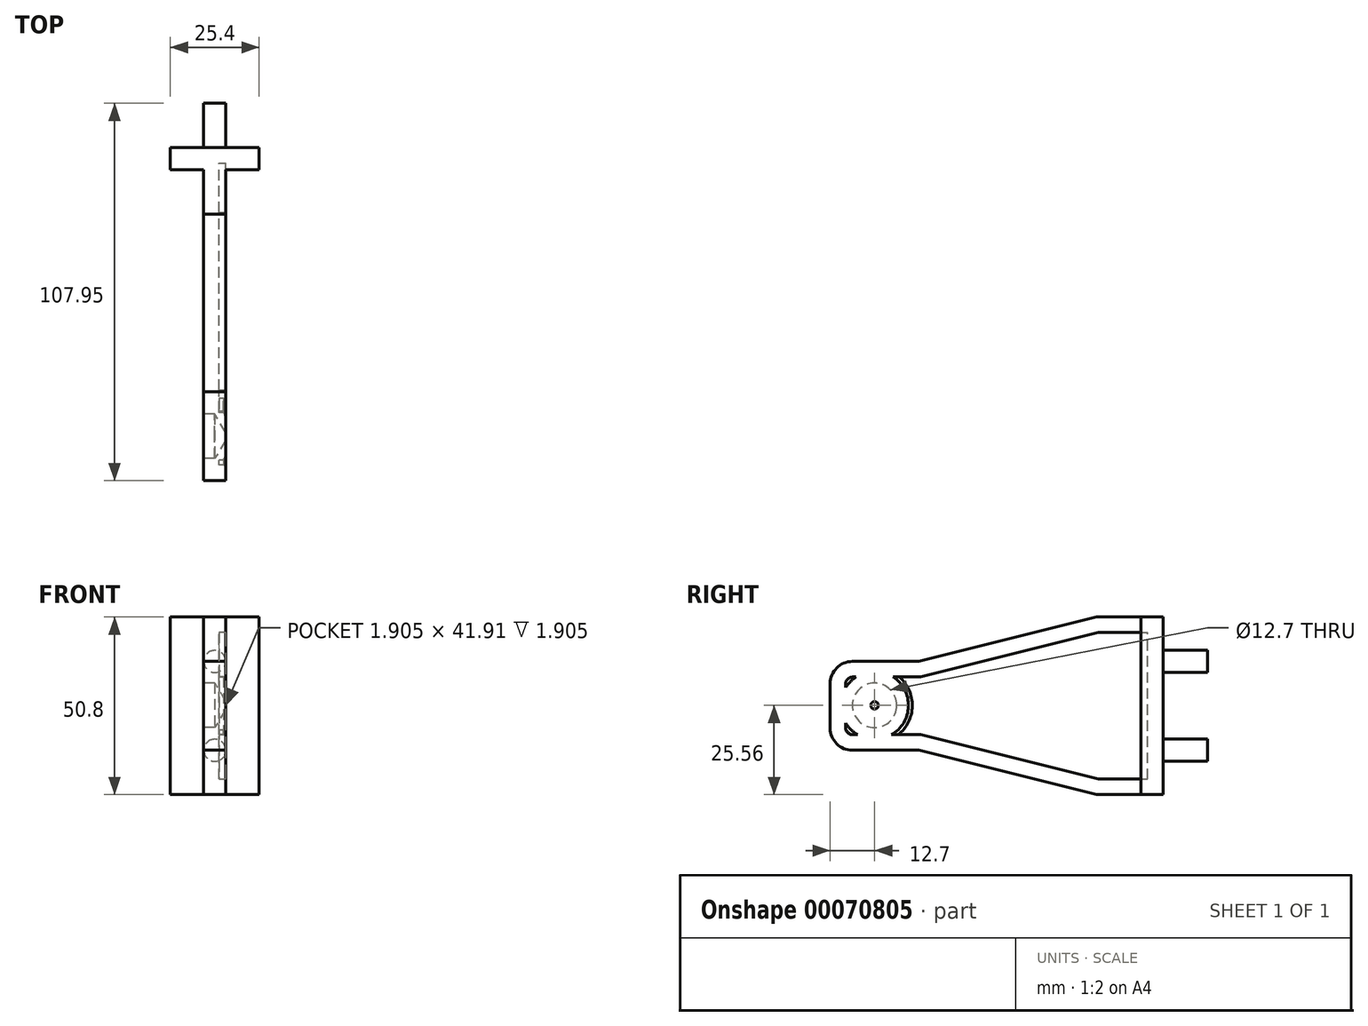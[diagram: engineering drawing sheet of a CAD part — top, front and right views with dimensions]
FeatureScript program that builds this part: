
annotation { "Feature Type Name" : "Feature", "Feature Type Description" : "" }
export const myFeature = defineFeature(function(context is Context, id is Id, definition is map)
    precondition{}
    {
        {
            var Q0;
            Q0=qCreatedBy(makeId("Front.planeOp"),FACE);
            var sketch = newSketch(context, id + "F0", { "sketchPlane" : qUnion([Q0])});
            skLineSegment(sketch, "E0.bottom", {"start": v(0, 0) * mm, "end": v(25.4, 0) * mm});
            skLineSegment(sketch, "E0.top", {"start": v(0, 50.8) * mm, "end": v(25.4, 50.8) * mm});
            skLineSegment(sketch, "E0.left", {"start": v(0, 0) * mm, "end": v(0, 50.8) * mm});
            skLineSegment(sketch, "E0.right", {"start": v(25.4, 0) * mm, "end": v(25.4, 50.8) * mm});
            skSolve(sketch);
        }
        {
            var Q0;
            Q0=makeQuery(id+"F0.imprint","IMPRINT",FACE,{"disambiguationData":[TD([[makeQuery(id+"F0.imprint","IMPRINT",EDGE,{"derivedFrom":sQuery(id+"F0.wireOp",EDGE,"E0.bottom")}),1.0]])]});
            extrude(context, id + "F1", {"entities" : qUnion([Q0]), "depth" : 6.35 * mm});
        }
        {
            var Q0;
            Q0=makeQuery(id+"F1.opExtrude","CAP_FACE",FACE,{"disambiguationData":[OSD([sQuery(id+"F0.wireOp",EDGE,"E0.bottom"),sQuery(id+"F0.wireOp",EDGE,"E0.top"),sQuery(id+"F0.wireOp",EDGE,"E0.left"),sQuery(id+"F0.wireOp",EDGE,"E0.right")])],"isStart":false});
            var sketch = newSketch(context, id + "F2", { "sketchPlane" : qUnion([Q0])});
            skLineSegment(sketch, "E1.bottom", {"start": v(9.53, 50.8) * mm, "end": v(15.88, 50.8) * mm});
            skLineSegment(sketch, "E1.top", {"start": v(9.53, 0) * mm, "end": v(15.88, 0) * mm});
            skLineSegment(sketch, "E1.left", {"start": v(9.53, 50.8) * mm, "end": v(9.53, 0) * mm});
            skLineSegment(sketch, "E1.right", {"start": v(15.88, 50.8) * mm, "end": v(15.88, 0) * mm});
            skSolve(sketch);
        }
        {
            var Q0;
            Q0=makeQuery(id+"F2.imprint","IMPRINT",FACE,{"disambiguationData":[TD([[makeQuery(id+"F2.imprint","IMPRINT",EDGE,{"derivedFrom":sQuery(id+"F2.wireOp",EDGE,"E1.bottom")}),-1.0]])]});
            extrude(context, id + "F3", {"entities" : qUnion([Q0]), "operationType" : NewBodyOperationType.ADD, "depth" : 12.7 * mm});
        }
        {
            var Q0;
            Q0=makeQuery(id+"F3.opExtrude","CAP_FACE",FACE,{"disambiguationData":[OSD([sQuery(id+"F2.wireOp",EDGE,"E1.bottom"),sQuery(id+"F2.wireOp",EDGE,"E1.top"),sQuery(id+"F2.wireOp",EDGE,"E1.left"),sQuery(id+"F2.wireOp",EDGE,"E1.right")])],"isStart":false});
            cPlane(context, id + "F4", {"entities" : qUnion([Q0]), "cplaneType" : CPlaneType.OFFSET, "offset" : 50.8 * mm, "width" : 152.4 * mm, "height" : 152.4 * mm});
        }
        {
            var Q0;
            Q0=qCreatedBy(id+"F4.planeOp",FACE);
            var sketch = newSketch(context, id + "F5", { "sketchPlane" : qUnion([Q0])});
            skLineSegment(sketch, "E2.0", {"start": v(9.53, 38.1) * mm, "end": v(9.53, 12.7) * mm});
            skLineSegment(sketch, "E3.0", {"start": v(15.88, 38.1) * mm, "end": v(15.88, 12.7) * mm});
            skLineSegment(sketch, "E4", {"start": v(9.53, 38.1) * mm, "end": v(15.88, 38.1) * mm});
            skLineSegment(sketch, "E5", {"start": v(9.53, 12.7) * mm, "end": v(15.88, 12.7) * mm});
            skSolve(sketch);
        }
        {
            var Q0;
            Q0=makeQuery(id+"F3.opExtrude","CAP_FACE",FACE,{"disambiguationData":[OSD([sQuery(id+"F2.wireOp",EDGE,"E1.bottom"),sQuery(id+"F2.wireOp",EDGE,"E1.top"),sQuery(id+"F2.wireOp",EDGE,"E1.left"),sQuery(id+"F2.wireOp",EDGE,"E1.right")])],"isStart":false});
            var Q1;
            Q1=makeQuery(id+"F5.imprint","IMPRINT",FACE,{"disambiguationData":[TD([[makeQuery(id+"F5.imprint","IMPRINT",EDGE,{"derivedFrom":sQuery(id+"F5.wireOp",EDGE,"E2.0")}),1.0]])]});
            loft(context, id + "F6", {"operationType" : NewBodyOperationType.ADD, "sheetProfilesArray" : [{ "sheetProfileEntities" : qUnion([Q0]) }, { "sheetProfileEntities" : qUnion([Q1]) }]});
        }
        {
            var Q0;
            Q0=makeQuery(id+"F6.opLoft","CAP_FACE",FACE,{"disambiguationData":[OSD([makeQuery(id+"F5.imprint","IMPRINT",FACE,{"disambiguationData":[TD([[makeQuery(id+"F5.imprint","IMPRINT",EDGE,{"derivedFrom":sQuery(id+"F5.wireOp",EDGE,"E2.0")}),1.0]])]})])],"isStart":true});
            extrude(context, id + "F7", {"entities" : qUnion([Q0]), "operationType" : NewBodyOperationType.ADD, "depth" : 25.4 * mm});
        }
        {
            var Q0;
            Q0=makeQuery(id+"F7.opExtrude","CAP_EDGE",EDGE,{"disambiguationData":[OSD([sQuery(id+"F5.wireOp",EDGE,"E2.0"),sQuery(id+"F5.wireOp",EDGE,"E3.0"),sQuery(id+"F5.wireOp",EDGE,"E4")])],"isStart":false});
            var Q1;
            Q1=makeQuery(id+"F7.opExtrude","CAP_EDGE",EDGE,{"disambiguationData":[OSD([sQuery(id+"F5.wireOp",EDGE,"E2.0"),sQuery(id+"F5.wireOp",EDGE,"E3.0"),sQuery(id+"F5.wireOp",EDGE,"E5")])],"isStart":false});
            fillet(context, id + "F8", {"entities" : qUnion([Q0, Q1]), "radius" : 6.35 * mm, "tangentPropagation" : true, "allowEdgeOverflow" : false});
        }
        {
            var Q0;
            {var subQ0=sQuery(id+"F5.wireOp",EDGE,"E5");var subQ1=sQuery(id+"F5.wireOp",EDGE,"E4");var subQ2=sQuery(id+"F5.wireOp",EDGE,"E2.0");var subQ3=sQuery(id+"F2.wireOp",EDGE,"E1.left");Q0=makeQuery(id+"F7.boolean.opBoolean","MERGE",FACE,{"derivedFrom":[makeQuery(id+"F6.boolean.opBoolean","MERGE",FACE,{"derivedFrom":[makeQuery(id+"F3.opExtrude","SWEPT_FACE",FACE,{"disambiguationData":[OSD([subQ3])]}),makeQuery(id+"F6.opLoft","SWEPT_FACE",FACE,{"disambiguationData":[OSD([sQuery(id+"F0.wireOp",EDGE,"E0.bottom"),sQuery(id+"F0.wireOp",EDGE,"E0.top"),sQuery(id+"F2.wireOp",EDGE,"E1.bottom"),sQuery(id+"F2.wireOp",EDGE,"E1.top"),subQ3,subQ2,subQ1,subQ0])]})]}),makeQuery(id+"F7.opExtrude","SWEPT_FACE",FACE,{"disambiguationData":[OSD([subQ2,subQ1,subQ0])]})]});}
            var sketch = newSketch(context, id + "F9", { "sketchPlane" : qUnion([Q0])});
            skPoint(sketch, "E6", {"position": v(95.25, 25.4) * mm});
            skPoint(sketch, "E7", {"position": v(82.55, 25.56) * mm});
            skSolve(sketch);
        }
        {
            var Q0;
            Q0=sQuery(id+"F9.wireOp",VERTEX,"E7");
            var Q1;
            Q1=makeQuery(id+"F1.opExtrude","SWEPT_BODY",BODY,{"disambiguationData":[OSD([sQuery(id+"F0.wireOp",EDGE,"E0.bottom"),sQuery(id+"F0.wireOp",EDGE,"E0.top"),sQuery(id+"F0.wireOp",EDGE,"E0.left"),sQuery(id+"F0.wireOp",EDGE,"E0.right")])]});
            hole(context, id + "F10", {"style" : HoleStyle.SIMPLE, "holeDiameter" : 12.7 * mm, "endStyle" : HoleEndStyle.BLIND, "holeDepth" : 3.17 * mm, "locations" : qUnion([Q0]), "scope" : qUnion([Q1])});
        }
        {
            var Q0;
            Q0=makeQuery(id+"F1.opExtrude","CAP_FACE",FACE,{"disambiguationData":[OSD([sQuery(id+"F0.wireOp",EDGE,"E0.bottom"),sQuery(id+"F0.wireOp",EDGE,"E0.top"),sQuery(id+"F0.wireOp",EDGE,"E0.left"),sQuery(id+"F0.wireOp",EDGE,"E0.right")])],"isStart":true});
            var sketch = newSketch(context, id + "F11", { "sketchPlane" : qUnion([Q0])});
            skCircle(sketch, "E8", {"center": v(-12.7, 38.1) * mm, "radius": 3.18 * mm});
            skPoint(sketch, "E8.centerSnap0", {"position": v(-12.7, 50.8) * mm});
            skCircle(sketch, "E9", {"center": v(-12.7, 12.7) * mm, "radius": 3.18 * mm});
            skPoint(sketch, "E9.centerSnap0", {"position": v(-12.7, 0) * mm});
            skSolve(sketch);
        }
        {
            var Q0;
            Q0=makeQuery(id+"F11.imprint","IMPRINT",FACE,{"disambiguationData":[TD([[makeQuery(id+"F11.imprint","IMPRINT",EDGE,{"derivedFrom":sQuery(id+"F11.wireOp",EDGE,"E8")}),1.0]])]});
            var Q1;
            Q1=makeQuery(id+"F11.imprint","IMPRINT",FACE,{"disambiguationData":[TD([[makeQuery(id+"F11.imprint","IMPRINT",EDGE,{"derivedFrom":sQuery(id+"F11.wireOp",EDGE,"E9")}),1.0]])]});
            extrude(context, id + "F12", {"entities" : qUnion([Q0, Q1]), "operationType" : NewBodyOperationType.ADD, "depth" : 12.7 * mm});
        }
        {
            var Q0;
            {var subQ0=sQuery(id+"F5.wireOp",EDGE,"E5");var subQ1=sQuery(id+"F5.wireOp",EDGE,"E4");var subQ2=sQuery(id+"F5.wireOp",EDGE,"E3.0");var subQ3=sQuery(id+"F2.wireOp",EDGE,"E1.right");Q0=makeQuery(id+"F7.boolean.opBoolean","MERGE",FACE,{"derivedFrom":[makeQuery(id+"F6.boolean.opBoolean","MERGE",FACE,{"derivedFrom":[makeQuery(id+"F3.opExtrude","SWEPT_FACE",FACE,{"disambiguationData":[OSD([subQ3])]}),makeQuery(id+"F6.opLoft","SWEPT_FACE",FACE,{"disambiguationData":[OSD([sQuery(id+"F0.wireOp",EDGE,"E0.bottom"),sQuery(id+"F0.wireOp",EDGE,"E0.top"),sQuery(id+"F2.wireOp",EDGE,"E1.bottom"),sQuery(id+"F2.wireOp",EDGE,"E1.top"),subQ3,subQ2,subQ1,subQ0])]})]}),makeQuery(id+"F7.opExtrude","SWEPT_FACE",FACE,{"disambiguationData":[OSD([subQ2,subQ1,subQ0])]})]});}
            shell(context, id + "F13", {"entities" : qUnion([Q0]), "thickness" : 4.44 * mm});
        }
    });
